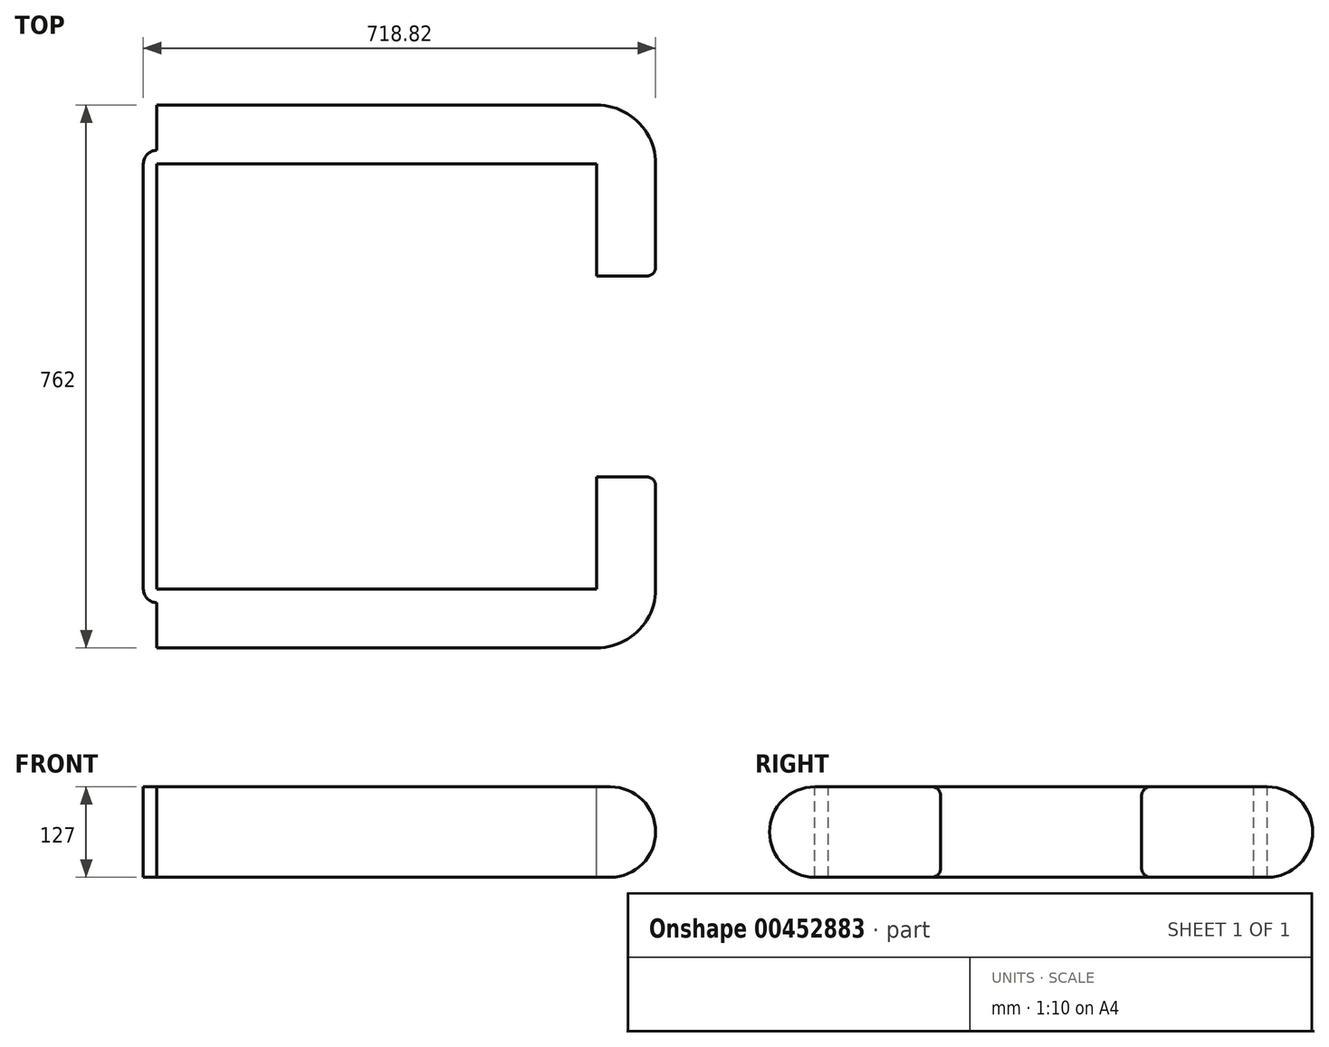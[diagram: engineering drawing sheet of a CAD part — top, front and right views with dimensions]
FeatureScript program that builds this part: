
annotation { "Feature Type Name" : "Feature", "Feature Type Description" : "" }
export const myFeature = defineFeature(function(context is Context, id is Id, definition is map)
    precondition{}
    {
        {
            var Q0;
            Q0=qCreatedBy(makeId("Front.planeOp"),FACE);
            var sketch = newSketch(context, id + "F0", { "sketchPlane" : qUnion([Q0])});
            skLineSegment(sketch, "E0.bottom", {"start": v(0, 0) * mm, "end": v(19.05, 0) * mm});
            skLineSegment(sketch, "E0.top", {"start": v(0, 127) * mm, "end": v(19.05, 127) * mm});
            skLineSegment(sketch, "E0.left", {"start": v(0, 0) * mm, "end": v(0, 127) * mm});
            skLineSegment(sketch, "E0.right", {"start": v(19.05, 0) * mm, "end": v(19.05, 127) * mm});
            skLineSegment(sketch, "E1", {"start": v(19.05, 63.5) * mm, "end": v(82.55, 63.5) * mm});
            skPoint(sketch, "E1.endSnap0", {"position": v(19.05, 63.5) * mm});
            skArc(sketch, "E2", {"start": v(82.55, 63.5) * mm, "mid": v(63.95, 108.4) * mm, "end": v(19.05, 127) * mm});
            skArc(sketch, "E3.MirrorCS", {"start": v(82.55, 63.5) * mm, "mid": v(63.95, 18.6) * mm, "end": v(19.05, 0) * mm});
            skLineSegment(sketch, "E4", {"start": v(129.66, 118.43) * mm, "end": v(129.66, -5.1) * mm});
            skArc(sketch, "E5.MirrorCS", {"start": v(176.78, 63.5) * mm, "mid": v(195.37, 108.4) * mm, "end": v(240.28, 127) * mm});
            skArc(sketch, "E6.MirrorCS", {"start": v(176.78, 63.5) * mm, "mid": v(195.37, 18.6) * mm, "end": v(240.28, 0) * mm});
            skLineSegment(sketch, "E7.MirrorCS", {"start": v(240.28, 0) * mm, "end": v(240.28, 127) * mm});
            skLineSegment(sketch, "E8.MirrorCS", {"start": v(259.33, 0) * mm, "end": v(259.33, 127) * mm});
            skLineSegment(sketch, "E9.MirrorCS", {"start": v(259.33, 0) * mm, "end": v(240.28, 0) * mm});
            skLineSegment(sketch, "E10.MirrorCS", {"start": v(259.33, 127) * mm, "end": v(240.28, 127) * mm});
            skArc(sketch, "E11.MirrorCS", {"start": v(-176.78, 63.5) * mm, "mid": v(-195.37, 108.4) * mm, "end": v(-240.28, 127) * mm});
            skLineSegment(sketch, "E12.MirrorCS", {"start": v(-240.28, 0) * mm, "end": v(-240.28, 127) * mm});
            skLineSegment(sketch, "E13.MirrorCS", {"start": v(-259.33, 0) * mm, "end": v(-259.33, 127) * mm});
            skLineSegment(sketch, "E14.MirrorCS", {"start": v(-259.33, 127) * mm, "end": v(-240.28, 127) * mm});
            skLineSegment(sketch, "E15.MirrorCS", {"start": v(-259.33, 0) * mm, "end": v(-240.28, 0) * mm});
            skArc(sketch, "E16.MirrorCS", {"start": v(-176.78, 63.5) * mm, "mid": v(-195.37, 18.6) * mm, "end": v(-240.28, 0) * mm});
            skSolve(sketch);
        }
        {
            var Q0;
            {var subQ2=sQuery(id+"F0.wireOp",EDGE,"E1");Q0=makeQuery(id+"F0.imprint","IMPRINT",FACE,{"disambiguationData":[TD([[makeQuery(id+"F0.imprint","IMPRINT",EDGE,{"derivedFrom":subQ2}),1.0]])]});}
            var Q1;
            {var subQ2=sQuery(id+"F0.wireOp",EDGE,"E1");Q1=makeQuery(id+"F0.imprint","IMPRINT",FACE,{"disambiguationData":[TD([[makeQuery(id+"F0.imprint","IMPRINT",EDGE,{"derivedFrom":subQ2}),-1.0]])]});}
            var Q2;
            {var subQ1=sQuery(id+"F0.wireOp",EDGE,"E0.bottom");Q2=makeQuery(id+"F0.imprint","IMPRINT",FACE,{"disambiguationData":[TD([[makeQuery(id+"F0.imprint","IMPRINT",EDGE,{"derivedFrom":subQ1}),1.0]])]});}
            extrude(context, id + "F1", {"entities" : qUnion([Q0, Q1, Q2]), "depth" : 617.22 * mm});
        }
        {
            var Q0;
            Q0=makeQuery(id+"F0.imprint","IMPRINT",FACE,{"disambiguationData":[TD([[makeQuery(id+"F0.imprint","IMPRINT",EDGE,{"derivedFrom":sQuery(id+"F0.wireOp",EDGE,"E7.MirrorCS")}),-1.0]])]});
            var Q1;
            Q1=makeQuery(id+"F0.imprint","IMPRINT",FACE,{"disambiguationData":[TD([[makeQuery(id+"F0.imprint","IMPRINT",EDGE,{"derivedFrom":sQuery(id+"F0.wireOp",EDGE,"E5.MirrorCS")}),-1.0]])]});
            extrude(context, id + "F2", {"entities" : qUnion([Q0, Q1]), "depth" : 596.9 * mm});
        }
        {
            var Q0;
            Q0=makeQuery(id+"F0.imprint","IMPRINT",FACE,{"disambiguationData":[TD([[makeQuery(id+"F0.imprint","IMPRINT",EDGE,{"derivedFrom":sQuery(id+"F0.wireOp",EDGE,"E11.MirrorCS")}),1.0]])]});
            var Q1;
            Q1=makeQuery(id+"F0.imprint","IMPRINT",FACE,{"disambiguationData":[TD([[makeQuery(id+"F0.imprint","IMPRINT",EDGE,{"derivedFrom":sQuery(id+"F0.wireOp",EDGE,"E12.MirrorCS")}),1.0]])]});
            extrude(context, id + "F3", {"entities" : qUnion([Q0, Q1]), "depth" : 152.4 * mm});
        }
        {
            var Q0;
            Q0=makeQuery(id+"F3.opExtrude","SWEPT_BODY",BODY,{"disambiguationData":[OSD([sQuery(id+"F0.wireOp",EDGE,"E11.MirrorCS"),sQuery(id+"F0.wireOp",EDGE,"E13.MirrorCS"),sQuery(id+"F0.wireOp",EDGE,"E14.MirrorCS"),sQuery(id+"F0.wireOp",EDGE,"E15.MirrorCS"),sQuery(id+"F0.wireOp",EDGE,"E16.MirrorCS")])]});
            transform(context, id + "F4", {"entities" : qUnion([Q0]), "transformType" : TransformType.TRANSLATION_3D, "dx" : 127 * mm, "dy" : 0 * mm, "dz" : 0 * mm, "makeCopy" : true});
        }
        {
            var Q0;
            Q0=makeQuery(id+"F1.opExtrude","SWEPT_BODY",BODY,{"disambiguationData":[OSD([sQuery(id+"F0.wireOp",EDGE,"E0.bottom"),sQuery(id+"F0.wireOp",EDGE,"E0.top"),sQuery(id+"F0.wireOp",EDGE,"E0.left"),sQuery(id+"F0.wireOp",EDGE,"E2"),sQuery(id+"F0.wireOp",EDGE,"E3.MirrorCS")])]});
            transform(context, id + "F5", {"entities" : qUnion([Q0]), "transformType" : TransformType.TRANSLATION_3D, "dx" : 127 * mm, "dy" : 127 * mm, "dz" : 254 * mm, "makeCopy" : true});
        }
        {
            var Q0;
            Q0=makeQuery(id+"F5.opPattern","COPY",BODY,{"derivedFrom":makeQuery(id+"F1.opExtrude","SWEPT_BODY",BODY,{"disambiguationData":[OSD([sQuery(id+"F0.wireOp",EDGE,"E0.bottom"),sQuery(id+"F0.wireOp",EDGE,"E0.top"),sQuery(id+"F0.wireOp",EDGE,"E0.left"),sQuery(id+"F0.wireOp",EDGE,"E2"),sQuery(id+"F0.wireOp",EDGE,"E3.MirrorCS")])]}),"instanceName":"1"});
            var Q1;
            Q1=makeQuery(id+"F5.opPattern","COPY",EDGE,{"derivedFrom":makeQuery(id+"F1.opExtrude","CAP_EDGE",EDGE,{"disambiguationData":[OSD([sQuery(id+"F0.wireOp",EDGE,"E0.left")])],"isStart":true}),"instanceName":"1"});
            transform(context, id + "F6", {"entities" : qUnion([Q0]), "transformType" : TransformType.ROTATION, "transformAxis" : qUnion([Q1]), "angle" : 90 * degree, "makeCopy" : false});
        }
        {
            var Q0;
            Q0=qCreatedBy(makeId("Right.planeOp"),FACE);
            var sketch = newSketch(context, id + "F7", { "sketchPlane" : qUnion([Q0])});
            skLineSegment(sketch, "E17.0", {"start": v(127, 254) * mm, "end": v(127, 381) * mm});
            skLineSegment(sketch, "E18.0", {"start": v(0, 0) * mm, "end": v(0, 127) * mm});
            skLineSegment(sketch, "E19", {"start": v(127, 254) * mm, "end": v(0, 0) * mm});
            skSolve(sketch);
        }
        {
            var Q0;
            Q0=qCreatedBy(makeId("Front.planeOp"),FACE);
            var sketch = newSketch(context, id + "F8", { "sketchPlane" : qUnion([Q0])});
            skLineSegment(sketch, "E20.0", {"start": v(259.33, 0) * mm, "end": v(259.33, 127) * mm});
            skLineSegment(sketch, "E21.0", {"start": v(0, 0) * mm, "end": v(0, 127) * mm});
            skLineSegment(sketch, "E22", {"start": v(0, 0) * mm, "end": v(259.33, 0) * mm});
            skSolve(sketch);
        }
        {
            var Q0;
            Q0=makeQuery(id+"F5.opPattern","COPY",BODY,{"derivedFrom":makeQuery(id+"F1.opExtrude","SWEPT_BODY",BODY,{"disambiguationData":[OSD([sQuery(id+"F0.wireOp",EDGE,"E0.bottom"),sQuery(id+"F0.wireOp",EDGE,"E0.top"),sQuery(id+"F0.wireOp",EDGE,"E0.left"),sQuery(id+"F0.wireOp",EDGE,"E2"),sQuery(id+"F0.wireOp",EDGE,"E3.MirrorCS")])]}),"instanceName":"1"});
            var Q1;
            Q1=sQuery(id+"F7.wireOp",VERTEX,"E19.start");
            var Q2;
            Q2=sQuery(id+"F8.wireOp",VERTEX,"E22.start");
            transform(context, id + "F9", {"entities" : qUnion([Q0]), "transformType" : TransformType.TRANSLATION_ENTITY, "oppositeDirectionEntity" : false, "transformLine" : qUnion([Q1, Q2]), "makeCopy" : false});
        }
        {
            var Q0;
            Q0=makeQuery(id+"F5.opPattern","COPY",FACE,{"derivedFrom":makeQuery(id+"F1.opExtrude","SWEPT_FACE",FACE,{"disambiguationData":[OSD([sQuery(id+"F0.wireOp",EDGE,"E0.bottom")])]}),"instanceName":"1"});
            var sketch = newSketch(context, id + "F10", { "sketchPlane" : qUnion([Q0])});
            skLineSegment(sketch, "E23.0", {"start": v(259.33, 0) * mm, "end": v(240.28, 0) * mm});
            skLineSegment(sketch, "E24", {"start": v(127, 0) * mm, "end": v(259.33, 0) * mm});
            skSolve(sketch);
        }
        {
            var Q0;
            Q0=makeQuery(id+"F5.opPattern","COPY",BODY,{"derivedFrom":makeQuery(id+"F1.opExtrude","SWEPT_BODY",BODY,{"disambiguationData":[OSD([sQuery(id+"F0.wireOp",EDGE,"E0.bottom"),sQuery(id+"F0.wireOp",EDGE,"E0.top"),sQuery(id+"F0.wireOp",EDGE,"E0.left"),sQuery(id+"F0.wireOp",EDGE,"E2"),sQuery(id+"F0.wireOp",EDGE,"E3.MirrorCS")])]}),"instanceName":"1"});
            var Q1;
            Q1=sQuery(id+"F10.wireOp",VERTEX,"E24.start");
            var Q2;
            Q2=sQuery(id+"F10.wireOp",VERTEX,"E23.0.start");
            transform(context, id + "F11", {"entities" : qUnion([Q0]), "transformType" : TransformType.TRANSLATION_ENTITY, "oppositeDirectionEntity" : false, "transformLine" : qUnion([Q1, Q2]), "makeCopy" : false});
        }
        {
            var Q0;
            Q0=makeQuery(id+"F1.opExtrude","SWEPT_BODY",BODY,{"disambiguationData":[OSD([sQuery(id+"F0.wireOp",EDGE,"E0.bottom"),sQuery(id+"F0.wireOp",EDGE,"E0.top"),sQuery(id+"F0.wireOp",EDGE,"E0.left"),sQuery(id+"F0.wireOp",EDGE,"E2"),sQuery(id+"F0.wireOp",EDGE,"E3.MirrorCS")])]});
            var Q1;
            Q1=makeQuery(id+"F1.opExtrude","CAP_EDGE",EDGE,{"disambiguationData":[OSD([sQuery(id+"F0.wireOp",EDGE,"E0.left")])],"isStart":false});
            transform(context, id + "F12", {"entities" : qUnion([Q0]), "transformType" : TransformType.ROTATION, "transformAxis" : qUnion([Q1]), "angle" : 90 * degree, "oppositeDirection" : true, "makeCopy" : false});
        }
        {
            var Q0;
            Q0=makeQuery(id+"F1.opExtrude","CAP_FACE",FACE,{"disambiguationData":[OSD([sQuery(id+"F0.wireOp",EDGE,"E0.bottom"),sQuery(id+"F0.wireOp",EDGE,"E0.top"),sQuery(id+"F0.wireOp",EDGE,"E0.left"),sQuery(id+"F0.wireOp",EDGE,"E2"),sQuery(id+"F0.wireOp",EDGE,"E3.MirrorCS")])],"isStart":false});
            var sketch = newSketch(context, id + "F13", { "sketchPlane" : qUnion([Q0])});
            skLineSegment(sketch, "E25.0", {"start": v(596.9, 0) * mm, "end": v(596.9, 127) * mm});
            skLineSegment(sketch, "E26", {"start": v(617.22, 0) * mm, "end": v(596.9, 0) * mm});
            skSolve(sketch);
        }
        {
            var Q0;
            Q0=makeQuery(id+"F1.opExtrude","SWEPT_BODY",BODY,{"disambiguationData":[OSD([sQuery(id+"F0.wireOp",EDGE,"E0.bottom"),sQuery(id+"F0.wireOp",EDGE,"E0.top"),sQuery(id+"F0.wireOp",EDGE,"E0.left"),sQuery(id+"F0.wireOp",EDGE,"E2"),sQuery(id+"F0.wireOp",EDGE,"E3.MirrorCS")])]});
            var Q1;
            Q1=sQuery(id+"F13.wireOp",VERTEX,"E26.start");
            var Q2;
            Q2=sQuery(id+"F13.wireOp",VERTEX,"E25.0.start");
            transform(context, id + "F14", {"entities" : qUnion([Q0]), "transformType" : TransformType.TRANSLATION_ENTITY, "oppositeDirectionEntity" : false, "transformLine" : qUnion([Q1, Q2]), "makeCopy" : false});
        }
        {
            var Q0;
            Q0=makeQuery(id+"F1.opExtrude","SWEPT_FACE",FACE,{"disambiguationData":[OSD([sQuery(id+"F0.wireOp",EDGE,"E0.bottom")])]});
            var sketch = newSketch(context, id + "F15", { "sketchPlane" : qUnion([Q0])});
            skLineSegment(sketch, "E27.0.0", {"start": v(240.28, 0) * mm, "end": v(259.33, 0) * mm});
            skLineSegment(sketch, "E27.0.1", {"start": v(259.33, 0) * mm, "end": v(259.33, 596.9) * mm});
            skLineSegment(sketch, "E27.0.2", {"start": v(259.33, 596.9) * mm, "end": v(240.28, 596.9) * mm});
            skLineSegment(sketch, "E27.0.3", {"start": v(240.28, 596.9) * mm, "end": v(240.28, 0) * mm});
            skLineSegment(sketch, "E28", {"start": v(0, 596.9) * mm, "end": v(259.33, 596.9) * mm});
            skSolve(sketch);
        }
        {
            var Q0;
            Q0=makeQuery(id+"F1.opExtrude","SWEPT_BODY",BODY,{"disambiguationData":[OSD([sQuery(id+"F0.wireOp",EDGE,"E0.bottom"),sQuery(id+"F0.wireOp",EDGE,"E0.top"),sQuery(id+"F0.wireOp",EDGE,"E0.left"),sQuery(id+"F0.wireOp",EDGE,"E2"),sQuery(id+"F0.wireOp",EDGE,"E3.MirrorCS")])]});
            var Q1;
            Q1=sQuery(id+"F15.wireOp",VERTEX,"E28.start");
            var Q2;
            Q2=sQuery(id+"F15.wireOp",VERTEX,"E27.0.1.end");
            transform(context, id + "F16", {"entities" : qUnion([Q0]), "transformType" : TransformType.TRANSLATION_ENTITY, "oppositeDirectionEntity" : false, "transformLine" : qUnion([Q1, Q2]), "makeCopy" : false});
        }
        {
            var Q0;
            Q0=makeQuery(id+"F2.opExtrude","SWEPT_FACE",FACE,{"disambiguationData":[OSD([sQuery(id+"F0.wireOp",EDGE,"E8.MirrorCS")])]});
            var sketch = newSketch(context, id + "F17", { "sketchPlane" : qUnion([Q0])});
            skLineSegment(sketch, "E29", {"start": v(-596.9, 127) * mm, "end": v(-596.9, 0) * mm});
            skSolve(sketch);
        }
        {
            var Q0;
            Q0=makeQuery(id+"F2.opExtrude","CAP_FACE",FACE,{"disambiguationData":[OSD([sQuery(id+"F0.wireOp",EDGE,"E5.MirrorCS"),sQuery(id+"F0.wireOp",EDGE,"E6.MirrorCS"),sQuery(id+"F0.wireOp",EDGE,"E8.MirrorCS"),sQuery(id+"F0.wireOp",EDGE,"E9.MirrorCS"),sQuery(id+"F0.wireOp",EDGE,"E10.MirrorCS")])],"isStart":false});
            var Q1;
            Q1=sQuery(id+"F17.wireOp",EDGE,"E29");
            revolve(context, id + "F18", {"operationType" : NewBodyOperationType.ADD, "entities" : qUnion([Q0]), "axis" : qUnion([Q1]), "revolveType" : RevolveType.ONE_DIRECTION, "oppositeDirection" : true, "angle" : 90 * degree});
        }
        {
            var Q0;
            Q0=makeQuery(id+"F0.imprint","IMPRINT",FACE,{"disambiguationData":[TD([[makeQuery(id+"F0.imprint","IMPRINT",EDGE,{"derivedFrom":sQuery(id+"F0.wireOp",EDGE,"E7.MirrorCS")}),-1.0]])]});
            var Q1;
            Q1=makeQuery(id+"F0.imprint","IMPRINT",FACE,{"disambiguationData":[TD([[makeQuery(id+"F0.imprint","IMPRINT",EDGE,{"derivedFrom":sQuery(id+"F0.wireOp",EDGE,"E5.MirrorCS")}),-1.0]])]});
            var Q2;
            Q2=sQuery(id+"F0.wireOp",EDGE,"E8.MirrorCS");
            revolve(context, id + "F19", {"operationType" : NewBodyOperationType.ADD, "entities" : qUnion([Q0, Q1]), "axis" : qUnion([Q2]), "revolveType" : RevolveType.ONE_DIRECTION, "oppositeDirection" : true, "angle" : 90 * degree});
        }
        {
            var Q0;
            Q0=makeQuery(id+"F4.opPattern","COPY",FACE,{"derivedFrom":makeQuery(id+"F3.opExtrude","SWEPT_FACE",FACE,{"disambiguationData":[OSD([sQuery(id+"F0.wireOp",EDGE,"E14.MirrorCS")])]}),"instanceName":"1"});
            var sketch = newSketch(context, id + "F20", { "sketchPlane" : qUnion([Q0])});
            skLineSegment(sketch, "E30.0", {"start": v(876.55, -596.9) * mm, "end": v(876.55, -615.95) * mm});
            skLineSegment(sketch, "E31", {"start": v(876.55, -596.9) * mm, "end": v(-132.33, -152.4) * mm});
            skLineSegment(sketch, "E32.0", {"start": v(876.55, 0) * mm, "end": v(876.55, 19.05) * mm});
            skLineSegment(sketch, "E33.0.0", {"start": v(-240.28, 0) * mm, "end": v(-259.33, 0) * mm});
            skLineSegment(sketch, "E33.0.1", {"start": v(-259.33, 0) * mm, "end": v(-259.33, -152.4) * mm});
            skLineSegment(sketch, "E33.0.2", {"start": v(-259.33, -152.4) * mm, "end": v(-240.28, -152.4) * mm});
            skLineSegment(sketch, "E33.0.3", {"start": v(-240.28, -152.4) * mm, "end": v(-240.28, 0) * mm});
            skLineSegment(sketch, "E34", {"start": v(-259.33, 0) * mm, "end": v(876.55, 0) * mm});
            skSolve(sketch);
        }
        {
            var Q0;
            Q0=makeQuery(id+"F4.opPattern","COPY",BODY,{"derivedFrom":makeQuery(id+"F3.opExtrude","SWEPT_BODY",BODY,{"disambiguationData":[OSD([sQuery(id+"F0.wireOp",EDGE,"E11.MirrorCS"),sQuery(id+"F0.wireOp",EDGE,"E13.MirrorCS"),sQuery(id+"F0.wireOp",EDGE,"E14.MirrorCS"),sQuery(id+"F0.wireOp",EDGE,"E15.MirrorCS"),sQuery(id+"F0.wireOp",EDGE,"E16.MirrorCS")])]}),"instanceName":"1"});
            var Q1;
            Q1=sQuery(id+"F20.wireOp",VERTEX,"E31.end");
            var Q2;
            Q2=sQuery(id+"F20.wireOp",VERTEX,"E30.0.start");
            transform(context, id + "F21", {"entities" : qUnion([Q0]), "transformType" : TransformType.TRANSLATION_ENTITY, "oppositeDirectionEntity" : false, "transformLine" : qUnion([Q1, Q2]), "makeCopy" : false});
        }
        {
            var Q0;
            Q0=makeQuery(id+"F3.opExtrude","SWEPT_BODY",BODY,{"disambiguationData":[OSD([sQuery(id+"F0.wireOp",EDGE,"E11.MirrorCS"),sQuery(id+"F0.wireOp",EDGE,"E13.MirrorCS"),sQuery(id+"F0.wireOp",EDGE,"E14.MirrorCS"),sQuery(id+"F0.wireOp",EDGE,"E15.MirrorCS"),sQuery(id+"F0.wireOp",EDGE,"E16.MirrorCS")])]});
            var Q1;
            Q1=sQuery(id+"F20.wireOp",VERTEX,"E34.start");
            var Q2;
            Q2=sQuery(id+"F20.wireOp",VERTEX,"E34.end");
            transform(context, id + "F22", {"entities" : qUnion([Q0]), "transformType" : TransformType.TRANSLATION_ENTITY, "oppositeDirectionEntity" : false, "transformLine" : qUnion([Q1, Q2]), "makeCopy" : false});
        }
        {
            var Q0;
            Q0=makeQuery(id+"F5.opPattern","COPY",FACE,{"derivedFrom":makeQuery(id+"F1.opExtrude","CAP_FACE",FACE,{"disambiguationData":[OSD([sQuery(id+"F0.wireOp",EDGE,"E0.bottom"),sQuery(id+"F0.wireOp",EDGE,"E0.top"),sQuery(id+"F0.wireOp",EDGE,"E0.left"),sQuery(id+"F0.wireOp",EDGE,"E2"),sQuery(id+"F0.wireOp",EDGE,"E3.MirrorCS")])],"isStart":false}),"instanceName":"1"});
            var Q1;
            Q1=makeQuery(id+"F5.opPattern","COPY",EDGE,{"derivedFrom":makeQuery(id+"F1.opExtrude","CAP_EDGE",EDGE,{"disambiguationData":[OSD([sQuery(id+"F0.wireOp",EDGE,"E0.left")])],"isStart":false}),"instanceName":"1"});
            revolve(context, id + "F23", {"operationType" : NewBodyOperationType.ADD, "entities" : qUnion([Q0]), "axis" : qUnion([Q1]), "revolveType" : RevolveType.ONE_DIRECTION, "oppositeDirection" : true, "angle" : 90 * degree});
        }
        {
            var Q0;
            Q0=makeQuery(id+"F1.opExtrude","CAP_FACE",FACE,{"disambiguationData":[OSD([sQuery(id+"F0.wireOp",EDGE,"E0.bottom"),sQuery(id+"F0.wireOp",EDGE,"E0.top"),sQuery(id+"F0.wireOp",EDGE,"E0.left"),sQuery(id+"F0.wireOp",EDGE,"E2"),sQuery(id+"F0.wireOp",EDGE,"E3.MirrorCS")])],"isStart":true});
            var Q1;
            Q1=makeQuery(id+"F1.opExtrude","CAP_EDGE",EDGE,{"disambiguationData":[OSD([sQuery(id+"F0.wireOp",EDGE,"E0.left")])],"isStart":true});
            revolve(context, id + "F24", {"operationType" : NewBodyOperationType.ADD, "entities" : qUnion([Q0]), "axis" : qUnion([Q1]), "revolveType" : RevolveType.ONE_DIRECTION, "angle" : 90 * degree});
        }
        {
            var Q0;
            Q0=makeQuery(id+"F4.opPattern","COPY",FACE,{"derivedFrom":makeQuery(id+"F3.opExtrude","CAP_FACE",FACE,{"disambiguationData":[OSD([sQuery(id+"F0.wireOp",EDGE,"E11.MirrorCS"),sQuery(id+"F0.wireOp",EDGE,"E13.MirrorCS"),sQuery(id+"F0.wireOp",EDGE,"E14.MirrorCS"),sQuery(id+"F0.wireOp",EDGE,"E15.MirrorCS"),sQuery(id+"F0.wireOp",EDGE,"E16.MirrorCS")])],"isStart":true}),"instanceName":"1"});
            extrude(context, id + "F25", {"entities" : qUnion([Q0]), "operationType" : NewBodyOperationType.ADD, "depth" : 5.08 * mm});
        }
        {
            var Q0;
            Q0=makeQuery(id+"F3.opExtrude","CAP_FACE",FACE,{"disambiguationData":[OSD([sQuery(id+"F0.wireOp",EDGE,"E11.MirrorCS"),sQuery(id+"F0.wireOp",EDGE,"E13.MirrorCS"),sQuery(id+"F0.wireOp",EDGE,"E14.MirrorCS"),sQuery(id+"F0.wireOp",EDGE,"E15.MirrorCS"),sQuery(id+"F0.wireOp",EDGE,"E16.MirrorCS")])],"isStart":false});
            extrude(context, id + "F26", {"entities" : qUnion([Q0]), "operationType" : NewBodyOperationType.ADD, "depth" : 5.08 * mm});
        }
        {
            var Q0;
            Q0=makeQuery(id+"F26.opExtrude","CAP_EDGE",EDGE,{"disambiguationData":[OSD([sQuery(id+"F0.wireOp",EDGE,"E11.MirrorCS"),sQuery(id+"F0.wireOp",EDGE,"E16.MirrorCS")])],"isStart":false});
            var Q1;
            Q1=makeQuery(id+"F25.opExtrude","CAP_EDGE",EDGE,{"disambiguationData":[OSD([sQuery(id+"F0.wireOp",EDGE,"E11.MirrorCS"),sQuery(id+"F0.wireOp",EDGE,"E16.MirrorCS")])],"isStart":false});
            fillet(context, id + "F27", {"entities" : qUnion([Q0, Q1]), "radius" : 12.7 * mm, "tangentPropagation" : true, "allowEdgeOverflow" : false});
        }
    });
